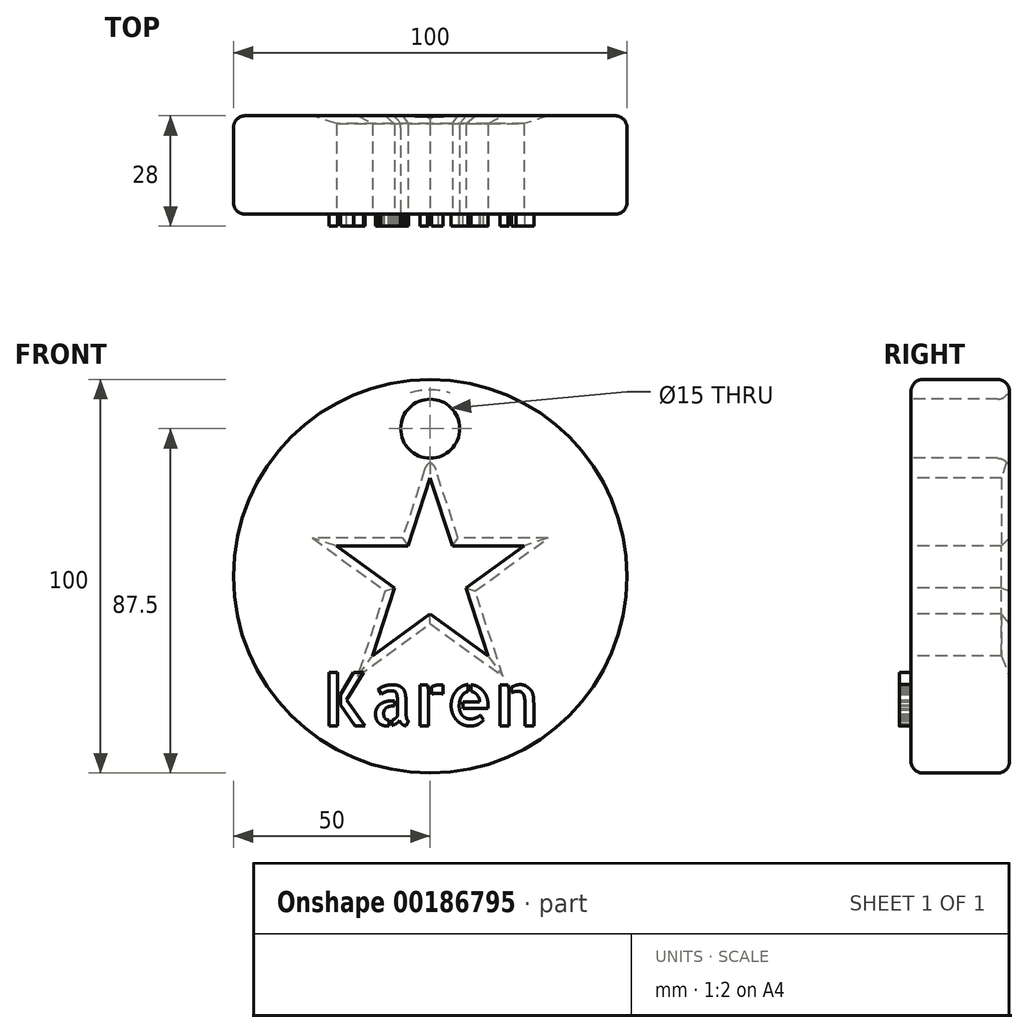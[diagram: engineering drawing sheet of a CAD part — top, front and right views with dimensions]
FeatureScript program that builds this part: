
annotation { "Feature Type Name" : "Feature", "Feature Type Description" : "" }
export const myFeature = defineFeature(function(context is Context, id is Id, definition is map)
    precondition{}
    {
        {
            var Q0;
            Q0=qCreatedBy(makeId("Front.planeOp"),FACE);
            var sketch = newSketch(context, id + "F0", { "sketchPlane" : qUnion([Q0])});
            skCircle(sketch, "E0", {"center": v(0, 0) * mm, "radius": 50 * mm});
            skSolve(sketch);
        }
        {
            var Q0;
            Q0 = qSketchRegion(id + "F0", true);
            extrude(context, id + "F1", {"entities" : qUnion([Q0]), "depth" : 12.5 * mm, "hasSecondDirection" : true, "secondDirectionOppositeDirection" : true, "secondDirectionDepth" : 12.5 * mm});
        }
        {
            var Q0;
            Q0=makeQuery(id+"F1.opExtrude","CAP_FACE",FACE,{"disambiguationData":[OSD([sQuery(id+"F0.wireOp",EDGE,"E0")])],"isStart":false});
            var sketch = newSketch(context, id + "F2", { "sketchPlane" : qUnion([Q0])});
            skCircle(sketch, "E1", {"center": v(0, 37.5) * mm, "radius": 7.5 * mm});
            skSolve(sketch);
        }
        {
            var Q0;
            Q0=makeQuery(id+"F2.imprint","IMPRINT",FACE,{"disambiguationData":[TD([[makeQuery(id+"F2.imprint","IMPRINT",EDGE,{"derivedFrom":sQuery(id+"F2.wireOp",EDGE,"E1")}),1.0]])]});
            extrude(context, id + "F3", {"entities" : qUnion([Q0]), "operationType" : NewBodyOperationType.REMOVE, "oppositeDirection" : true, "depth" : 26 * mm});
        }
        {
            var Q0;
            Q0=makeQuery(id+"F1.opExtrude","CAP_FACE",FACE,{"disambiguationData":[OSD([sQuery(id+"F0.wireOp",EDGE,"E0")])],"isStart":false});
            var sketch = newSketch(context, id + "F4", { "sketchPlane" : qUnion([Q0])});
            skArc(sketch, "E2.cCircle", {"start": v(-18.7, 7.73) * mm, "mid": v(-19.24, 6.25) * mm, "end": v(-19.66, 4.74) * mm, "construction": true});
            skLineSegment(sketch, "E2.0", {"start": v(0, 25) * mm, "end": v(23.78, 7.73) * mm});
            skLineSegment(sketch, "E2.1", {"start": v(23.78, 7.73) * mm, "end": v(14.7, -20.23) * mm});
            skLineSegment(sketch, "E2.2", {"start": v(14.7, -20.23) * mm, "end": v(-14.7, -20.23) * mm});
            skLineSegment(sketch, "E2.3", {"start": v(-14.7, -20.23) * mm, "end": v(-23.78, 7.73) * mm});
            skLineSegment(sketch, "E2.4", {"start": v(-23.78, 7.73) * mm, "end": v(0, 25) * mm});
            skPoint(sketch, "E2.0.midPoint", {"position": v(11.89, 16.36) * mm});
            skLineSegment(sketch, "E3", {"start": v(0, 25) * mm, "end": v(-5.61, 7.73) * mm});
            skLineSegment(sketch, "E4", {"start": v(0, 25) * mm, "end": v(5.61, 7.73) * mm});
            skLineSegment(sketch, "E5", {"start": v(23.78, 7.73) * mm, "end": v(5.61, 7.73) * mm});
            skLineSegment(sketch, "E6", {"start": v(-23.78, 7.73) * mm, "end": v(-9.08, -2.95) * mm});
            skLineSegment(sketch, "E7", {"start": v(-14.7, -20.23) * mm, "end": v(0, -9.55) * mm});
            skLineSegment(sketch, "E8.trimOffspring", {"start": v(-9.08, -2.95) * mm, "end": v(-14.7, -20.23) * mm});
            skLineSegment(sketch, "E9.trimOffspring", {"start": v(-5.61, 7.73) * mm, "end": v(-23.78, 7.73) * mm});
            skLineSegment(sketch, "E10.trimOffspring", {"start": v(9.08, -2.95) * mm, "end": v(14.7, -20.23) * mm});
            skLineSegment(sketch, "E11.trimOffspring", {"start": v(9.08, -2.95) * mm, "end": v(23.78, 7.73) * mm});
            skLineSegment(sketch, "E12.trimOffspring", {"start": v(0, -9.55) * mm, "end": v(14.7, -20.23) * mm});
            skArc(sketch, "E13.trimOffspring", {"start": v(-13.12, -15.39) * mm, "mid": v(-11.89, -16.36) * mm, "end": v(-10.58, -17.24) * mm, "construction": true});
            skArc(sketch, "E14.trimOffspring", {"start": v(10.58, -17.24) * mm, "mid": v(11.89, -16.36) * mm, "end": v(13.12, -15.39) * mm, "construction": true});
            skArc(sketch, "E15.trimOffspring", {"start": v(19.66, 4.74) * mm, "mid": v(19.24, 6.25) * mm, "end": v(18.7, 7.73) * mm, "construction": true});
            skArc(sketch, "E16.trimOffspring", {"start": v(1.57, 20.16) * mm, "mid": v(0, 20.23) * mm, "end": v(-1.57, 20.16) * mm, "construction": true});
            skSolve(sketch);
        }
        {
            var Q0;
            Q0=makeQuery(id+"F4.imprint","IMPRINT",FACE,{"disambiguationData":[TD([[makeQuery(id+"F4.imprint","IMPRINT",EDGE,{"derivedFrom":sQuery(id+"F4.wireOp",EDGE,"E3")}),1.0]])]});
            extrude(context, id + "F5", {"entities" : qUnion([Q0]), "operationType" : NewBodyOperationType.REMOVE, "oppositeDirection" : true, "depth" : 26 * mm});
        }
        {
            var Q0;
            Q0=makeQuery(id+"F1.opExtrude","CAP_FACE",FACE,{"disambiguationData":[OSD([sQuery(id+"F0.wireOp",EDGE,"E0")])],"isStart":false});
            var sketch = newSketch(context, id + "F6", { "sketchPlane" : qUnion([Q0])});
            skText(sketch, "E17", { "text": "Karen", "fontName": "AllertaStencil-Regular.ttf"});
            const initialGuessF6  = {"E17": [-0.02745, -0.03797, 1, 0, 0.01352]};
            skSetInitialGuess(sketch, initialGuessF6);
            skSolve(sketch);
        }
        {
            var Q0;
            Q0 = qSketchRegion(id + "F6", true);
            extrude(context, id + "F7", {"entities" : qUnion([Q0]), "operationType" : NewBodyOperationType.ADD, "depth" : 3 * mm});
        }
        {
            var Q0;
            Q0=makeQuery(id+"F5.boolean.opBoolean","COPY",EDGE,{"derivedFrom":makeQuery(id+"F5.opExtrude","CAP_EDGE",EDGE,{"disambiguationData":[OSD([sQuery(id+"F4.wireOp",EDGE,"E3")])],"isStart":true})});
            var Q1;
            Q1=makeQuery(id+"F5.boolean.opBoolean","COPY",EDGE,{"derivedFrom":makeQuery(id+"F5.opExtrude","CAP_EDGE",EDGE,{"disambiguationData":[OSD([sQuery(id+"F4.wireOp",EDGE,"E4")])],"isStart":true})});
            var Q2;
            Q2=makeQuery(id+"F5.boolean.opBoolean","COPY",EDGE,{"derivedFrom":makeQuery(id+"F5.opExtrude","CAP_EDGE",EDGE,{"disambiguationData":[OSD([sQuery(id+"F4.wireOp",EDGE,"E5")])],"isStart":true})});
            var Q3;
            Q3=makeQuery(id+"F5.boolean.opBoolean","COPY",EDGE,{"derivedFrom":makeQuery(id+"F5.opExtrude","CAP_EDGE",EDGE,{"disambiguationData":[OSD([sQuery(id+"F4.wireOp",EDGE,"E11.trimOffspring")])],"isStart":true})});
            var Q4;
            Q4=makeQuery(id+"F5.boolean.opBoolean","COPY",EDGE,{"derivedFrom":makeQuery(id+"F5.opExtrude","CAP_EDGE",EDGE,{"disambiguationData":[OSD([sQuery(id+"F4.wireOp",EDGE,"E10.trimOffspring")])],"isStart":true})});
            var Q5;
            Q5=makeQuery(id+"F5.boolean.opBoolean","COPY",EDGE,{"derivedFrom":makeQuery(id+"F5.opExtrude","CAP_EDGE",EDGE,{"disambiguationData":[OSD([sQuery(id+"F4.wireOp",EDGE,"E12.trimOffspring")])],"isStart":true})});
            var Q6;
            Q6=makeQuery(id+"F5.boolean.opBoolean","COPY",EDGE,{"derivedFrom":makeQuery(id+"F5.opExtrude","CAP_EDGE",EDGE,{"disambiguationData":[OSD([sQuery(id+"F4.wireOp",EDGE,"E7")])],"isStart":true})});
            var Q7;
            Q7=makeQuery(id+"F5.boolean.opBoolean","COPY",EDGE,{"derivedFrom":makeQuery(id+"F5.opExtrude","CAP_EDGE",EDGE,{"disambiguationData":[OSD([sQuery(id+"F4.wireOp",EDGE,"E8.trimOffspring")])],"isStart":true})});
            var Q8;
            Q8=makeQuery(id+"F5.boolean.opBoolean","COPY",EDGE,{"derivedFrom":makeQuery(id+"F5.opExtrude","CAP_EDGE",EDGE,{"disambiguationData":[OSD([sQuery(id+"F4.wireOp",EDGE,"E6")])],"isStart":true})});
            var Q9;
            Q9=makeQuery(id+"F5.boolean.opBoolean","COPY",EDGE,{"derivedFrom":makeQuery(id+"F5.opExtrude","CAP_EDGE",EDGE,{"disambiguationData":[OSD([sQuery(id+"F4.wireOp",EDGE,"E9.trimOffspring")])],"isStart":true})});
            var Q10;
            Q10=makeQuery(id+"F5.boolean.opBoolean","INTERSECT",EDGE,{"derivedFrom":[makeQuery(id+"F1.opExtrude","CAP_FACE",FACE,{"disambiguationData":[OSD([sQuery(id+"F0.wireOp",EDGE,"E0")])],"isStart":true}),makeQuery(id+"F5.opExtrude","SWEPT_FACE",FACE,{"disambiguationData":[OSD([sQuery(id+"F4.wireOp",EDGE,"E11.trimOffspring")])]})]});
            var Q11;
            Q11=makeQuery(id+"F5.boolean.opBoolean","INTERSECT",EDGE,{"derivedFrom":[makeQuery(id+"F1.opExtrude","CAP_FACE",FACE,{"disambiguationData":[OSD([sQuery(id+"F0.wireOp",EDGE,"E0")])],"isStart":true}),makeQuery(id+"F5.opExtrude","SWEPT_FACE",FACE,{"disambiguationData":[OSD([sQuery(id+"F4.wireOp",EDGE,"E5")])]})]});
            var Q12;
            Q12=makeQuery(id+"F5.boolean.opBoolean","INTERSECT",EDGE,{"derivedFrom":[makeQuery(id+"F1.opExtrude","CAP_FACE",FACE,{"disambiguationData":[OSD([sQuery(id+"F0.wireOp",EDGE,"E0")])],"isStart":true}),makeQuery(id+"F5.opExtrude","SWEPT_FACE",FACE,{"disambiguationData":[OSD([sQuery(id+"F4.wireOp",EDGE,"E4")])]})]});
            var Q13;
            Q13=makeQuery(id+"F5.boolean.opBoolean","INTERSECT",EDGE,{"derivedFrom":[makeQuery(id+"F1.opExtrude","CAP_FACE",FACE,{"disambiguationData":[OSD([sQuery(id+"F0.wireOp",EDGE,"E0")])],"isStart":true}),makeQuery(id+"F5.opExtrude","SWEPT_FACE",FACE,{"disambiguationData":[OSD([sQuery(id+"F4.wireOp",EDGE,"E3")])]})]});
            var Q14;
            Q14=makeQuery(id+"F5.boolean.opBoolean","INTERSECT",EDGE,{"derivedFrom":[makeQuery(id+"F1.opExtrude","CAP_FACE",FACE,{"disambiguationData":[OSD([sQuery(id+"F0.wireOp",EDGE,"E0")])],"isStart":true}),makeQuery(id+"F5.opExtrude","SWEPT_FACE",FACE,{"disambiguationData":[OSD([sQuery(id+"F4.wireOp",EDGE,"E9.trimOffspring")])]})]});
            var Q15;
            Q15=makeQuery(id+"F5.boolean.opBoolean","INTERSECT",EDGE,{"derivedFrom":[makeQuery(id+"F1.opExtrude","CAP_FACE",FACE,{"disambiguationData":[OSD([sQuery(id+"F0.wireOp",EDGE,"E0")])],"isStart":true}),makeQuery(id+"F5.opExtrude","SWEPT_FACE",FACE,{"disambiguationData":[OSD([sQuery(id+"F4.wireOp",EDGE,"E6")])]})]});
            var Q16;
            Q16=makeQuery(id+"F5.boolean.opBoolean","INTERSECT",EDGE,{"derivedFrom":[makeQuery(id+"F1.opExtrude","CAP_FACE",FACE,{"disambiguationData":[OSD([sQuery(id+"F0.wireOp",EDGE,"E0")])],"isStart":true}),makeQuery(id+"F5.opExtrude","SWEPT_FACE",FACE,{"disambiguationData":[OSD([sQuery(id+"F4.wireOp",EDGE,"E8.trimOffspring")])]})]});
            var Q17;
            Q17=makeQuery(id+"F5.boolean.opBoolean","INTERSECT",EDGE,{"derivedFrom":[makeQuery(id+"F1.opExtrude","CAP_FACE",FACE,{"disambiguationData":[OSD([sQuery(id+"F0.wireOp",EDGE,"E0")])],"isStart":true}),makeQuery(id+"F5.opExtrude","SWEPT_FACE",FACE,{"disambiguationData":[OSD([sQuery(id+"F4.wireOp",EDGE,"E7")])]})]});
            var Q18;
            Q18=makeQuery(id+"F5.boolean.opBoolean","INTERSECT",EDGE,{"derivedFrom":[makeQuery(id+"F1.opExtrude","CAP_FACE",FACE,{"disambiguationData":[OSD([sQuery(id+"F0.wireOp",EDGE,"E0")])],"isStart":true}),makeQuery(id+"F5.opExtrude","SWEPT_FACE",FACE,{"disambiguationData":[OSD([sQuery(id+"F4.wireOp",EDGE,"E12.trimOffspring")])]})]});
            var Q19;
            Q19=makeQuery(id+"F5.boolean.opBoolean","INTERSECT",EDGE,{"derivedFrom":[makeQuery(id+"F1.opExtrude","CAP_FACE",FACE,{"disambiguationData":[OSD([sQuery(id+"F0.wireOp",EDGE,"E0")])],"isStart":true}),makeQuery(id+"F5.opExtrude","SWEPT_FACE",FACE,{"disambiguationData":[OSD([sQuery(id+"F4.wireOp",EDGE,"E10.trimOffspring")])]})]});
            chamfer(context, id + "F8", {"entities" : qUnion([Q0, Q1, Q2, Q3, Q4, Q5, Q6, Q7, Q8, Q9, Q10, Q11, Q12, Q13, Q14, Q15, Q16, Q17, Q18, Q19]), "width" : 2 * mm, "tangentPropagation" : true});
        }
        {
            var Q0;
            Q0=makeQuery(id+"F1.opExtrude","CAP_EDGE",EDGE,{"disambiguationData":[OSD([sQuery(id+"F0.wireOp",EDGE,"E0")])],"isStart":false});
            var Q1;
            Q1=makeQuery(id+"F1.opExtrude","CAP_EDGE",EDGE,{"disambiguationData":[OSD([sQuery(id+"F0.wireOp",EDGE,"E0")])],"isStart":true});
            var Q2;
            Q2=makeQuery(id+"F3.boolean.opBoolean","COPY",EDGE,{"derivedFrom":makeQuery(id+"F3.opExtrude","CAP_EDGE",EDGE,{"disambiguationData":[OSD([sQuery(id+"F2.wireOp",EDGE,"E1")])],"isStart":true})});
            var Q3;
            Q3=makeQuery(id+"F3.boolean.opBoolean","INTERSECT",EDGE,{"derivedFrom":[makeQuery(id+"F1.opExtrude","CAP_FACE",FACE,{"disambiguationData":[OSD([sQuery(id+"F0.wireOp",EDGE,"E0")])],"isStart":true}),makeQuery(id+"F3.opExtrude","SWEPT_FACE",FACE,{"disambiguationData":[OSD([sQuery(id+"F2.wireOp",EDGE,"E1")])]})]});
            fillet(context, id + "F9", {"entities" : qUnion([Q0, Q1, Q2, Q3]), "radius" : 3 * mm, "tangentPropagation" : true, "allowEdgeOverflow" : false});
        }
    });
